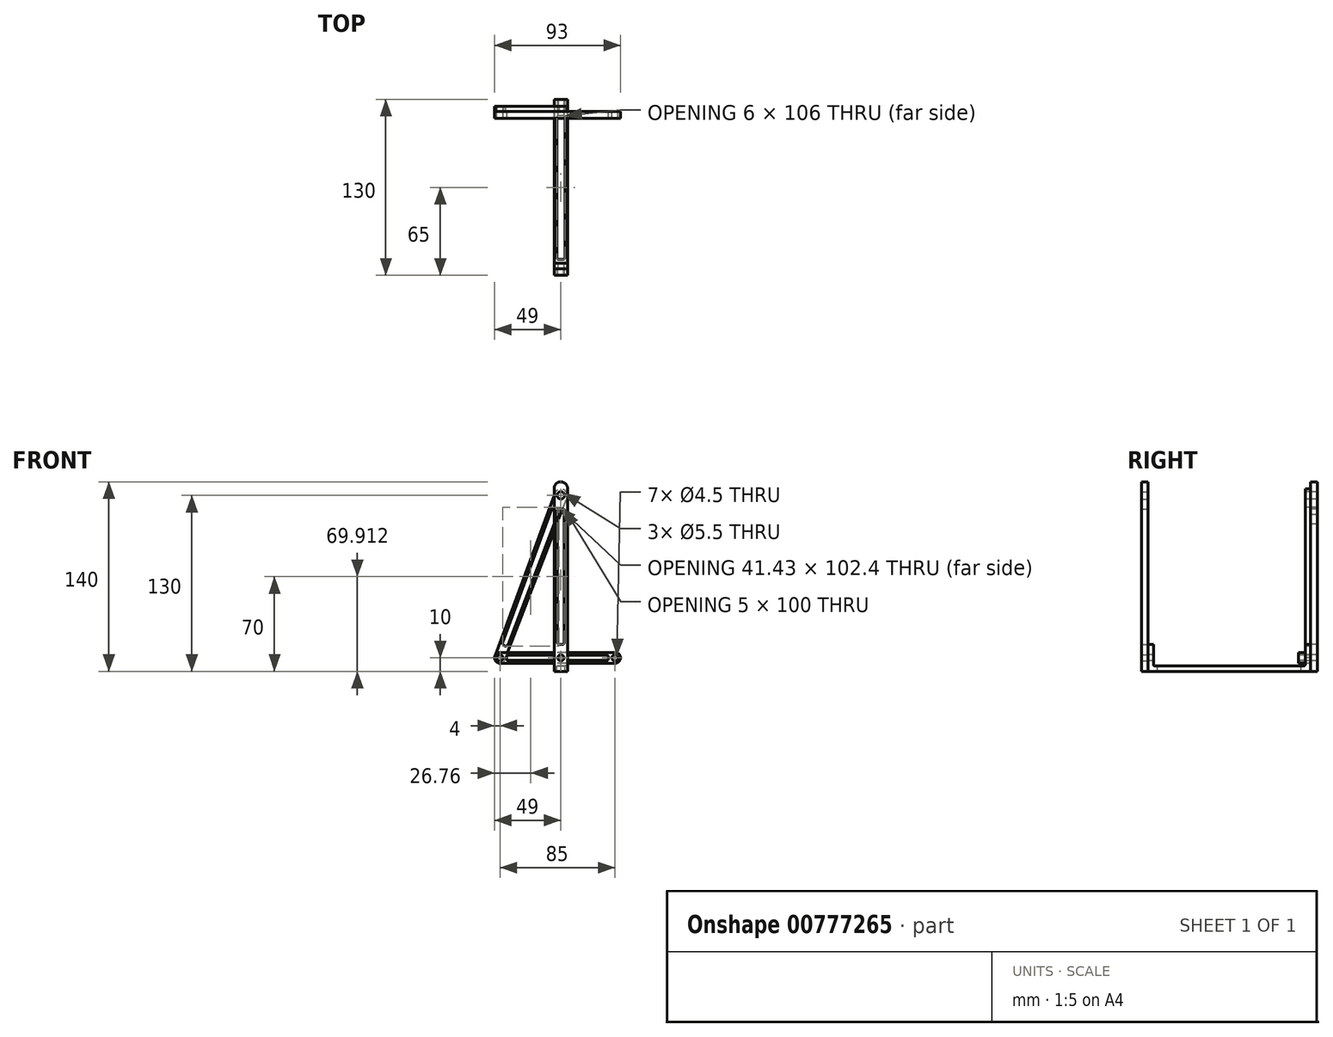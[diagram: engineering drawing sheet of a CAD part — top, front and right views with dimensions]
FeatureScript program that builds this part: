
annotation { "Feature Type Name" : "Feature", "Feature Type Description" : "" }
export const myFeature = defineFeature(function(context is Context, id is Id, definition is map)
    precondition{}
    {
        {
            var Q0;
            Q0=qCreatedBy(makeId("Front.planeOp"),FACE);
            var sketch = newSketch(context, id + "F0", { "sketchPlane" : qUnion([Q0])});
            skLineSegment(sketch, "E0", {"start": v(0, 0) * mm, "end": v(10, 0) * mm});
            skLineSegment(sketch, "E1", {"start": v(10, 0) * mm, "end": v(10, 135) * mm});
            skLineSegment(sketch, "E2", {"start": v(5, 140) * mm, "end": v(5, 140) * mm});
            skLineSegment(sketch, "E3", {"start": v(0, 135) * mm, "end": v(0, 0) * mm});
            skLineSegment(sketch, "E4", {"start": v(5, 140) * mm, "end": v(5, 130) * mm});
            skLineSegment(sketch, "E5", {"start": v(5, 130) * mm, "end": v(5, 10) * mm});
            skCircle(sketch, "E6", {"center": v(5, 130) * mm, "radius": 2.75 * mm});
            skCircle(sketch, "E7", {"center": v(5, 10) * mm, "radius": 2.25 * mm});
            skLineSegment(sketch, "E8", {"start": v(0, 70) * mm, "end": v(10, 70) * mm});
            skLineSegment(sketch, "E9.bottom", {"start": v(6.5, 20) * mm, "end": v(3.5, 20) * mm});
            skLineSegment(sketch, "E9.top", {"start": v(6.5, 120) * mm, "end": v(3.5, 120) * mm});
            skLineSegment(sketch, "E9.left", {"start": v(7.5, 21) * mm, "end": v(7.5, 119) * mm});
            skLineSegment(sketch, "E9.right", {"start": v(2.5, 21) * mm, "end": v(2.5, 119) * mm});
            skPoint(sketch, "E9.middle", {"position": v(5, 70) * mm});
            skPoint(sketch, "E10.visualSharp", {"position": v(0, 140) * mm});
            skArc(sketch, "E10.filletArc", {"start": v(5, 140) * mm, "mid": v(1.46, 138.54) * mm, "end": v(0, 135) * mm});
            skPoint(sketch, "E11.visualSharp", {"position": v(10, 140) * mm});
            skArc(sketch, "E11.filletArc", {"start": v(10, 135) * mm, "mid": v(8.54, 138.54) * mm, "end": v(5, 140) * mm});
            skPoint(sketch, "E12.visualSharp", {"position": v(2.5, 20) * mm});
            skArc(sketch, "E12.filletArc", {"start": v(2.5, 21) * mm, "mid": v(2.8, 20.3) * mm, "end": v(3.5, 20) * mm});
            skPoint(sketch, "E13.visualSharp", {"position": v(7.5, 20) * mm});
            skArc(sketch, "E13.filletArc", {"start": v(6.5, 20) * mm, "mid": v(7.2, 20.3) * mm, "end": v(7.5, 21) * mm});
            skPoint(sketch, "E14.visualSharp", {"position": v(2.5, 120) * mm});
            skArc(sketch, "E14.filletArc", {"start": v(3.5, 120) * mm, "mid": v(2.8, 119.7) * mm, "end": v(2.5, 119) * mm});
            skPoint(sketch, "E15.visualSharp", {"position": v(7.5, 120) * mm});
            skArc(sketch, "E15.filletArc", {"start": v(7.5, 119) * mm, "mid": v(7.2, 119.7) * mm, "end": v(6.5, 120) * mm});
            skSolve(sketch);
        }
        {
            var Q0;
            {var subQ5=sQuery(id+"F0.wireOp",EDGE,"E11.filletArc");Q0=makeQuery(id+"F0.imprint","IMPRINT",FACE,{"disambiguationData":[TD([[makeQuery(id+"F0.imprint","IMPRINT",EDGE,{"derivedFrom":subQ5}),1.0]])]});}
            var Q1;
            {var subQ5=sQuery(id+"F0.wireOp",EDGE,"E10.filletArc");Q1=makeQuery(id+"F0.imprint","IMPRINT",FACE,{"disambiguationData":[TD([[makeQuery(id+"F0.imprint","IMPRINT",EDGE,{"derivedFrom":subQ5}),1.0]])]});}
            var Q2;
            {var subQ13=sQuery(id+"F0.wireOp",EDGE,"E0");Q2=makeQuery(id+"F0.imprint","IMPRINT",FACE,{"disambiguationData":[TD([[makeQuery(id+"F0.imprint","IMPRINT",EDGE,{"derivedFrom":subQ13}),1.0]])]});}
            extrude(context, id + "F1", {"entities" : qUnion([Q0, Q1, Q2]), "depth" : 5 * mm, "offsetDistance" : 25 * mm});
        }
        {
            var Q0;
            Q0=qCreatedBy(makeId("Right.planeOp"),FACE);
            var sketch = newSketch(context, id + "F2", { "sketchPlane" : qUnion([Q0])});
            skLineSegment(sketch, "E16", {"start": v(0, 0) * mm, "end": v(60, 0) * mm});
            skLineSegment(sketch, "E17", {"start": v(60, 0) * mm, "end": v(60, 100) * mm});
            skSolve(sketch);
        }
        {
            var Q0;
            Q0=sQuery(id+"F2.wireOp",EDGE,"E17");
            cPlane(context, id + "F3", {"entities" : qUnion([Q0]), "cplaneType" : CPlaneType.LINE_ANGLE, "offset" : 25 * mm, "angle" : 90 * degree, "width" : 150 * mm, "height" : 150 * mm});
        }
        {
            var Q0;
            Q0=makeQuery(id+"F1.opExtrude","SWEPT_BODY",BODY,{"disambiguationData":[OSD([sQuery(id+"F0.wireOp",EDGE,"E0"),sQuery(id+"F0.wireOp",EDGE,"E1"),sQuery(id+"F0.wireOp",EDGE,"E3"),sQuery(id+"F0.wireOp",EDGE,"E6"),sQuery(id+"F0.wireOp",EDGE,"E7"),sQuery(id+"F0.wireOp",EDGE,"E9.bottom"),sQuery(id+"F0.wireOp",EDGE,"E9.top"),sQuery(id+"F0.wireOp",EDGE,"E9.left"),sQuery(id+"F0.wireOp",EDGE,"E9.right"),sQuery(id+"F0.wireOp",EDGE,"E10.filletArc"),sQuery(id+"F0.wireOp",EDGE,"E11.filletArc"),sQuery(id+"F0.wireOp",EDGE,"E12.filletArc"),sQuery(id+"F0.wireOp",EDGE,"E13.filletArc"),sQuery(id+"F0.wireOp",EDGE,"E14.filletArc"),sQuery(id+"F0.wireOp",EDGE,"E15.filletArc")])]});
            var Q1;
            Q1=qCreatedBy(id+"F3.planeOp",FACE);
            mirror(context, id + "F4", {"entities" : qUnion([Q0]), "mirrorPlane" : qUnion([Q1])});
        }
        {
            var Q0;
            Q0=qCreatedBy(makeId("Right.planeOp"),FACE);
            var sketch = newSketch(context, id + "F5", { "sketchPlane" : qUnion([Q0])});
            skLineSegment(sketch, "E18", {"start": v(0, 0) * mm, "end": v(120, 0) * mm});
            skLineSegment(sketch, "E19", {"start": v(120, 0) * mm, "end": v(120, 20) * mm});
            skLineSegment(sketch, "E20", {"start": v(120, 20) * mm, "end": v(0, 20) * mm});
            skLineSegment(sketch, "E21", {"start": v(0, 20) * mm, "end": v(0, 0) * mm});
            skLineSegment(sketch, "E22.0", {"start": v(116, 5) * mm, "end": v(116, 15) * mm});
            skLineSegment(sketch, "E22.1", {"start": v(5, 4) * mm, "end": v(115, 4) * mm});
            skLineSegment(sketch, "E22.2", {"start": v(4, 15) * mm, "end": v(4, 5) * mm});
            skPoint(sketch, "E23.visualSharp", {"position": v(116, 16) * mm});
            skPoint(sketch, "E24.visualSharp", {"position": v(4, 4) * mm});
            skArc(sketch, "E24.filletArc", {"start": v(4, 5) * mm, "mid": v(4.3, 4.3) * mm, "end": v(5, 4) * mm});
            skPoint(sketch, "E25.visualSharp", {"position": v(116, 4) * mm});
            skArc(sketch, "E25.filletArc", {"start": v(115, 4) * mm, "mid": v(115.7, 4.3) * mm, "end": v(116, 5) * mm});
            skLineSegment(sketch, "E26", {"start": v(116, 15) * mm, "end": v(116, 20) * mm});
            skLineSegment(sketch, "E27", {"start": v(4, 15) * mm, "end": v(4, 20) * mm});
            skSolve(sketch);
        }
        {
            var Q0;
            Q0=makeQuery(id+"F5.imprint","IMPRINT",FACE,{"disambiguationData":[TD([[makeQuery(id+"F5.imprint","IMPRINT",EDGE,{"derivedFrom":sQuery(id+"F5.wireOp",EDGE,"E18")}),1.0]])]});
            extrude(context, id + "F6", {"entities" : qUnion([Q0]), "depth" : 10 * mm, "offsetDistance" : 25 * mm});
        }
        {
            var Q0;
            Q0=makeQuery(id+"F6.opExtrude","SWEPT_FACE",FACE,{"disambiguationData":[OSD([sQuery(id+"F5.wireOp",EDGE,"E22.1")])]});
            var sketch = newSketch(context, id + "F7", { "sketchPlane" : qUnion([Q0])});
            skLineSegment(sketch, "E28.0", {"start": v(2, 112) * mm, "end": v(2, 8) * mm});
            skLineSegment(sketch, "E28.1", {"start": v(7, 113) * mm, "end": v(3, 113) * mm});
            skLineSegment(sketch, "E28.2", {"start": v(8, 8) * mm, "end": v(8, 112) * mm});
            skLineSegment(sketch, "E28.3", {"start": v(3, 7) * mm, "end": v(7, 7) * mm});
            skPoint(sketch, "E29.visualSharp", {"position": v(2, 7) * mm});
            skArc(sketch, "E29.filletArc", {"start": v(2, 8) * mm, "mid": v(2.3, 7.3) * mm, "end": v(3, 7) * mm});
            skPoint(sketch, "E30.visualSharp", {"position": v(8, 7) * mm});
            skArc(sketch, "E30.filletArc", {"start": v(7, 7) * mm, "mid": v(7.7, 7.3) * mm, "end": v(8, 8) * mm});
            skPoint(sketch, "E31.visualSharp", {"position": v(8, 113) * mm});
            skArc(sketch, "E31.filletArc", {"start": v(8, 112) * mm, "mid": v(7.7, 112.7) * mm, "end": v(7, 113) * mm});
            skPoint(sketch, "E32.visualSharp", {"position": v(2, 113) * mm});
            skArc(sketch, "E32.filletArc", {"start": v(3, 113) * mm, "mid": v(2.3, 112.7) * mm, "end": v(2, 112) * mm});
            skSolve(sketch);
        }
        {
            var Q0;
            Q0=makeQuery(id+"F7.imprint","IMPRINT",FACE,{"disambiguationData":[TD([[makeQuery(id+"F7.imprint","IMPRINT",EDGE,{"derivedFrom":sQuery(id+"F7.wireOp",EDGE,"E28.0")}),1.0]])]});
            extrude(context, id + "F8", {"entities" : qUnion([Q0]), "operationType" : NewBodyOperationType.REMOVE, "oppositeDirection" : true, "depth" : 25 * mm, "offsetDistance" : 25 * mm});
        }
        {
            var Q0;
            Q0=makeQuery(id+"F1.opExtrude","CAP_FACE",FACE,{"disambiguationData":[OSD([sQuery(id+"F0.wireOp",EDGE,"E0"),sQuery(id+"F0.wireOp",EDGE,"E1"),sQuery(id+"F0.wireOp",EDGE,"E3"),sQuery(id+"F0.wireOp",EDGE,"E6"),sQuery(id+"F0.wireOp",EDGE,"E7"),sQuery(id+"F0.wireOp",EDGE,"E9.bottom"),sQuery(id+"F0.wireOp",EDGE,"E9.top"),sQuery(id+"F0.wireOp",EDGE,"E9.left"),sQuery(id+"F0.wireOp",EDGE,"E9.right"),sQuery(id+"F0.wireOp",EDGE,"E10.filletArc"),sQuery(id+"F0.wireOp",EDGE,"E11.filletArc"),sQuery(id+"F0.wireOp",EDGE,"E12.filletArc"),sQuery(id+"F0.wireOp",EDGE,"E13.filletArc"),sQuery(id+"F0.wireOp",EDGE,"E14.filletArc"),sQuery(id+"F0.wireOp",EDGE,"E15.filletArc")])],"isStart":false});
            var sketch = newSketch(context, id + "F9", { "sketchPlane" : qUnion([Q0])});
            skCircle(sketch, "E33.0", {"center": v(5, 10) * mm, "radius": 2.25 * mm});
            skSolve(sketch);
        }
        {
            var Q0;
            Q0=makeQuery(id+"F9.imprint","IMPRINT",FACE,{"disambiguationData":[TD([[makeQuery(id+"F9.imprint","IMPRINT",EDGE,{"derivedFrom":sQuery(id+"F9.wireOp",EDGE,"E33.0")}),1.0]])]});
            extrude(context, id + "F10", {"entities" : qUnion([Q0]), "operationType" : NewBodyOperationType.REMOVE, "endBound" : BoundingType.THROUGH_ALL, "oppositeDirection" : true, "depth" : 25 * mm, "offsetDistance" : 25 * mm});
        }
        {
            var Q0;
            Q0=makeQuery(id+"F6.opExtrude","SWEPT_FACE",FACE,{"disambiguationData":[OSD([sQuery(id+"F5.wireOp",EDGE,"E22.0"),sQuery(id+"F5.wireOp",EDGE,"E26")])]});
            var sketch = newSketch(context, id + "F11", { "sketchPlane" : qUnion([Q0])});
            skCircle(sketch, "E34", {"center": v(5, 10) * mm, "radius": 4 * mm});
            skLineSegment(sketch, "E35", {"start": v(5, 10) * mm, "end": v(5, 14) * mm});
            skLineSegment(sketch, "E36", {"start": v(5, 14) * mm, "end": v(0, 14) * mm});
            skLineSegment(sketch, "E37", {"start": v(5, 10) * mm, "end": v(5, 6) * mm});
            skLineSegment(sketch, "E38", {"start": v(5, 6) * mm, "end": v(0, 6) * mm});
            skLineSegment(sketch, "E39", {"start": v(0, 6) * mm, "end": v(-40, 6) * mm});
            skLineSegment(sketch, "E40", {"start": v(-40, 6) * mm, "end": v(-40, 10) * mm});
            skCircle(sketch, "E41", {"center": v(-40, 10) * mm, "radius": 4 * mm});
            skCircle(sketch, "E42", {"center": v(-40, 10) * mm, "radius": 2.25 * mm});
            skLineSegment(sketch, "E43", {"start": v(0, 14) * mm, "end": v(-40, 14) * mm});
            skLineSegment(sketch, "E44", {"start": v(-40, 10) * mm, "end": v(-35, 10) * mm});
            skLineSegment(sketch, "E45", {"start": v(-35, 10) * mm, "end": v(-45, 10) * mm});
            skLineSegment(sketch, "E46", {"start": v(5, 14) * mm, "end": v(45, 14) * mm});
            skLineSegment(sketch, "E47", {"start": v(45, 14) * mm, "end": v(45, 9) * mm});
            skLineSegment(sketch, "E48", {"start": v(45, 9) * mm, "end": v(45, 6) * mm});
            skLineSegment(sketch, "E49", {"start": v(45, 6) * mm, "end": v(5, 6) * mm});
            skCircle(sketch, "E50", {"center": v(45, 10) * mm, "radius": 4 * mm});
            skCircle(sketch, "E51", {"center": v(45, 10) * mm, "radius": 2.25 * mm});
            skLineSegment(sketch, "E52.bottom", {"start": v(39, 8) * mm, "end": v(11, 8) * mm});
            skLineSegment(sketch, "E52.top", {"start": v(39, 12) * mm, "end": v(11, 12) * mm});
            skLineSegment(sketch, "E52.left", {"start": v(40, 9) * mm, "end": v(40, 11) * mm});
            skLineSegment(sketch, "E52.right", {"start": v(10, 9) * mm, "end": v(10, 11) * mm});
            skPoint(sketch, "E52.middle", {"position": v(25, 10) * mm});
            skPoint(sketch, "E52.middle.positionSnap0", {"position": v(25, 14) * mm});
            skPoint(sketch, "E52.centerSnap0", {"position": v(25, 14) * mm});
            skPoint(sketch, "E53.visualSharp", {"position": v(10, 12) * mm});
            skArc(sketch, "E53.filletArc", {"start": v(11, 12) * mm, "mid": v(10.3, 11.7) * mm, "end": v(10, 11) * mm});
            skPoint(sketch, "E54.visualSharp", {"position": v(10, 8) * mm});
            skArc(sketch, "E54.filletArc", {"start": v(10, 9) * mm, "mid": v(10.3, 8.3) * mm, "end": v(11, 8) * mm});
            skPoint(sketch, "E55.visualSharp", {"position": v(40, 8) * mm});
            skArc(sketch, "E55.filletArc", {"start": v(39, 8) * mm, "mid": v(39.7, 8.3) * mm, "end": v(40, 9) * mm});
            skPoint(sketch, "E56.visualSharp", {"position": v(40, 12) * mm});
            skArc(sketch, "E56.filletArc", {"start": v(40, 11) * mm, "mid": v(39.7, 11.7) * mm, "end": v(39, 12) * mm});
            skSolve(sketch);
        }
        {
            var Q0;
            {var subQ0=sQuery(id+"F11.wireOp",EDGE,"E35");var subQ1=sQuery(id+"F11.wireOp",EDGE,"E34");var subQ2=makeQuery(id+"F11.imprint","INTERSECT",VERTEX,{"derivedFrom":[subQ1,subQ0,sQuery(id+"F11.wireOp",EDGE,"E36")]});Q0=makeQuery(id+"F11.imprint","IMPRINT",FACE,{"disambiguationData":[TD([[makeQuery(id+"F11.imprint","IMPRINT",EDGE,{"disambiguationData":[TD([[subQ2,-1.0]])],"derivedFrom":subQ1}),1.0]])]});}
            var Q1;
            {var subQ0=sQuery(id+"F11.wireOp",EDGE,"E35");var subQ1=sQuery(id+"F11.wireOp",EDGE,"E34");var subQ2=makeQuery(id+"F11.imprint","INTERSECT",VERTEX,{"derivedFrom":[subQ1,subQ0,sQuery(id+"F11.wireOp",EDGE,"E36")]});Q1=makeQuery(id+"F11.imprint","IMPRINT",FACE,{"disambiguationData":[TD([[makeQuery(id+"F11.imprint","IMPRINT",EDGE,{"disambiguationData":[TD([[subQ2,1.0]])],"derivedFrom":subQ1}),1.0]])]});}
            var Q2;
            {var subQ0=sQuery(id+"F11.wireOp",EDGE,"E36");Q2=makeQuery(id+"F11.imprint","IMPRINT",FACE,{"disambiguationData":[TD([[makeQuery(id+"F11.imprint","IMPRINT",EDGE,{"derivedFrom":subQ0}),1.0]])]});}
            var Q3;
            {var subQ1=sQuery(id+"F11.wireOp",EDGE,"E39");Q3=makeQuery(id+"F11.imprint","IMPRINT",FACE,{"disambiguationData":[TD([[makeQuery(id+"F11.imprint","IMPRINT",EDGE,{"derivedFrom":subQ1}),-1.0]])]});}
            var Q4;
            {var subQ1=sQuery(id+"F11.wireOp",EDGE,"E40");var subQ3=sQuery(id+"F11.wireOp",EDGE,"E42");var subQ4=makeQuery(id+"F11.imprint","INTERSECT",VERTEX,{"derivedFrom":[subQ1,subQ3]});Q4=makeQuery(id+"F11.imprint","IMPRINT",FACE,{"disambiguationData":[TD([[makeQuery(id+"F11.imprint","IMPRINT",EDGE,{"disambiguationData":[TD([[subQ4,-1.0]])],"derivedFrom":subQ3}),-1.0]])]});}
            var Q5;
            {var subQ1=sQuery(id+"F11.wireOp",EDGE,"E40");var subQ3=sQuery(id+"F11.wireOp",EDGE,"E42");var subQ4=makeQuery(id+"F11.imprint","INTERSECT",VERTEX,{"derivedFrom":[subQ1,subQ3]});Q5=makeQuery(id+"F11.imprint","IMPRINT",FACE,{"disambiguationData":[TD([[makeQuery(id+"F11.imprint","IMPRINT",EDGE,{"disambiguationData":[TD([[subQ4,1.0]])],"derivedFrom":subQ3}),-1.0]])]});}
            var Q6;
            {var subQ1=sQuery(id+"F11.wireOp",EDGE,"E41");var subQ6=makeQuery(id+"F11.imprint","INTERSECT",VERTEX,{"derivedFrom":[subQ1,sQuery(id+"F11.wireOp",EDGE,"E43")]});Q6=makeQuery(id+"F11.imprint","IMPRINT",FACE,{"disambiguationData":[TD([[makeQuery(id+"F11.imprint","IMPRINT",EDGE,{"disambiguationData":[TD([[subQ6,1.0]])],"derivedFrom":subQ1}),1.0]])]});}
            extrude(context, id + "F12", {"entities" : qUnion([Q0, Q1, Q2, Q3, Q4, Q5, Q6]), "depth" : 5 * mm, "offsetDistance" : 25 * mm});
        }
        {
            var Q0;
            Q0=makeQuery(id+"F12.opExtrude","CAP_FACE",FACE,{"disambiguationData":[OSD([sQuery(id+"F5.wireOp",EDGE,"E22.0"),sQuery(id+"F5.wireOp",EDGE,"E26"),sQuery(id+"F9.wireOp",EDGE,"E33.0"),sQuery(id+"F11.wireOp",EDGE,"E34"),sQuery(id+"F11.wireOp",EDGE,"E36"),sQuery(id+"F11.wireOp",EDGE,"E38"),sQuery(id+"F11.wireOp",EDGE,"E39"),sQuery(id+"F11.wireOp",EDGE,"E41"),sQuery(id+"F11.wireOp",EDGE,"E42"),sQuery(id+"F11.wireOp",EDGE,"E43")])],"isStart":false});
            var sketch = newSketch(context, id + "F13", { "sketchPlane" : qUnion([Q0])});
            skCircle(sketch, "E57", {"center": v(5, 10) * mm, "radius": 2 * mm});
            skLineSegment(sketch, "E58", {"start": v(-40, 10) * mm, "end": v(5, 10) * mm});
            skLineSegment(sketch, "E59.bottom", {"start": v(-1, 8) * mm, "end": v(-34, 8) * mm});
            skLineSegment(sketch, "E59.top", {"start": v(-1, 12) * mm, "end": v(-34, 12) * mm});
            skLineSegment(sketch, "E59.left", {"start": v(0, 9) * mm, "end": v(0, 11) * mm});
            skLineSegment(sketch, "E59.right", {"start": v(-35, 9) * mm, "end": v(-35, 11) * mm});
            skPoint(sketch, "E59.middle", {"position": v(-17.5, 10) * mm});
            skPoint(sketch, "E60.visualSharp", {"position": v(-35, 12) * mm});
            skArc(sketch, "E60.filletArc", {"start": v(-34, 12) * mm, "mid": v(-34.7, 11.7) * mm, "end": v(-35, 11) * mm});
            skPoint(sketch, "E61.visualSharp", {"position": v(-35, 8) * mm});
            skArc(sketch, "E61.filletArc", {"start": v(-35, 9) * mm, "mid": v(-34.7, 8.3) * mm, "end": v(-34, 8) * mm});
            skPoint(sketch, "E62.visualSharp", {"position": v(0, 8) * mm});
            skArc(sketch, "E62.filletArc", {"start": v(-1, 8) * mm, "mid": v(-0.3, 8.3) * mm, "end": v(0, 9) * mm});
            skPoint(sketch, "E63.visualSharp", {"position": v(0, 12) * mm});
            skArc(sketch, "E63.filletArc", {"start": v(0, 11) * mm, "mid": v(-0.3, 11.7) * mm, "end": v(-1, 12) * mm});
            skSolve(sketch);
        }
        {
            var Q0;
            Q0=makeQuery(id+"F13.imprint","IMPRINT",FACE,{"disambiguationData":[TD([[makeQuery(id+"F13.imprint","IMPRINT",EDGE,{"derivedFrom":sQuery(id+"F13.wireOp",EDGE,"E59.top")}),1.0]])]});
            var Q1;
            Q1=makeQuery(id+"F13.imprint","IMPRINT",FACE,{"disambiguationData":[TD([[makeQuery(id+"F13.imprint","IMPRINT",EDGE,{"derivedFrom":sQuery(id+"F13.wireOp",EDGE,"E59.bottom")}),-1.0]])]});
            extrude(context, id + "F14", {"entities" : qUnion([Q0, Q1]), "operationType" : NewBodyOperationType.REMOVE, "oppositeDirection" : true, "depth" : 25 * mm, "offsetDistance" : 25 * mm});
        }
        {
            var Q0;
            Q0=makeQuery(id+"F12.opExtrude","SWEPT_BODY",BODY,{"disambiguationData":[OSD([sQuery(id+"F5.wireOp",EDGE,"E22.0"),sQuery(id+"F5.wireOp",EDGE,"E26"),sQuery(id+"F9.wireOp",EDGE,"E33.0"),sQuery(id+"F11.wireOp",EDGE,"E34"),sQuery(id+"F11.wireOp",EDGE,"E36"),sQuery(id+"F11.wireOp",EDGE,"E38"),sQuery(id+"F11.wireOp",EDGE,"E39"),sQuery(id+"F11.wireOp",EDGE,"E41"),sQuery(id+"F11.wireOp",EDGE,"E42"),sQuery(id+"F11.wireOp",EDGE,"E43")])]});
            transform(context, id + "F15", {"entities" : qUnion([Q0]), "transformType" : TransformType.TRANSLATION_3D, "dx" : 0 * mm, "dy" : 0 * mm, "dz" : 0 * mm, "makeCopy" : true});
        }
        {
            var Q0;
            {var subQ0=sQuery(id+"F11.wireOp",EDGE,"E50");var subQ1=sQuery(id+"F11.wireOp",EDGE,"E46");var subQ2=makeQuery(id+"F11.imprint","INTERSECT",VERTEX,{"derivedFrom":[subQ1,sQuery(id+"F11.wireOp",EDGE,"E47"),subQ0]});Q0=makeQuery(id+"F11.imprint","IMPRINT",FACE,{"disambiguationData":[TD([[makeQuery(id+"F11.imprint","IMPRINT",EDGE,{"disambiguationData":[TD([[subQ2,1.0]])],"derivedFrom":subQ1}),-1.0]])]});}
            var Q1;
            {var subQ0=sQuery(id+"F11.wireOp",EDGE,"E46");var subQ5=makeQuery(id+"F6.opExtrude","CAP_EDGE",EDGE,{"disambiguationData":[OSD([sQuery(id+"F5.wireOp",EDGE,"E22.0"),sQuery(id+"F5.wireOp",EDGE,"E26")])],"isStart":false});var subQ6=makeQuery(id+"F11.imprint","INTERSECT",VERTEX,{"derivedFrom":[subQ5,subQ0]});Q1=makeQuery(id+"F11.imprint","IMPRINT",FACE,{"disambiguationData":[TD([[makeQuery(id+"F11.imprint","IMPRINT",EDGE,{"disambiguationData":[TD([[subQ6,1.0]])],"derivedFrom":subQ0}),-1.0]])]});}
            var Q2;
            {var subQ1=sQuery(id+"F11.wireOp",EDGE,"E47");var subQ3=sQuery(id+"F11.wireOp",EDGE,"E51");var subQ4=makeQuery(id+"F11.imprint","INTERSECT",VERTEX,{"derivedFrom":[subQ1,subQ3]});Q2=makeQuery(id+"F11.imprint","IMPRINT",FACE,{"disambiguationData":[TD([[makeQuery(id+"F11.imprint","IMPRINT",EDGE,{"disambiguationData":[TD([[subQ4,-1.0]])],"derivedFrom":subQ3}),-1.0]])]});}
            var Q3;
            {var subQ1=sQuery(id+"F11.wireOp",EDGE,"E47");var subQ3=sQuery(id+"F11.wireOp",EDGE,"E51");var subQ4=makeQuery(id+"F11.imprint","INTERSECT",VERTEX,{"derivedFrom":[subQ1,subQ3]});Q3=makeQuery(id+"F11.imprint","IMPRINT",FACE,{"disambiguationData":[TD([[makeQuery(id+"F11.imprint","IMPRINT",EDGE,{"disambiguationData":[TD([[subQ4,1.0]])],"derivedFrom":subQ3}),-1.0]])]});}
            extrude(context, id + "F16", {"entities" : qUnion([Q0, Q1, Q2, Q3]), "operationType" : NewBodyOperationType.ADD, "depth" : 5 * mm, "offsetDistance" : 25 * mm});
        }
        {
            var Q0;
            {var subQ1=sQuery(id+"F11.wireOp",EDGE,"E39");Q0=makeQuery(id+"F11.imprint","IMPRINT",FACE,{"disambiguationData":[TD([[makeQuery(id+"F11.imprint","IMPRINT",EDGE,{"derivedFrom":subQ1}),-1.0]])]});}
            var sketch = newSketch(context, id + "F17", { "sketchPlane" : qUnion([Q0])});
            skCircle(sketch, "E64.0", {"center": v(-40, 10) * mm, "radius": 2.25 * mm});
            skCircle(sketch, "E65.0", {"center": v(-40, 10) * mm, "radius": 4 * mm});
            skCircle(sketch, "E66.0", {"center": v(5, 130) * mm, "radius": 2.75 * mm});
            skCircle(sketch, "E67.0", {"center": v(5, 130) * mm, "radius": 4.75 * mm});
            skLineSegment(sketch, "E68", {"start": v(-43.48, 11.98) * mm, "end": v(0.54, 131.64) * mm});
            skLineSegment(sketch, "E69", {"start": v(-36, 10) * mm, "end": v(9.43, 128.3) * mm});
            skSolve(sketch);
        }
        {
            var Q0;
            {var subQ5=sQuery(id+"F17.wireOp",EDGE,"E68");Q0=makeQuery(id+"F17.imprint","IMPRINT",FACE,{"disambiguationData":[TD([[makeQuery(id+"F17.imprint","IMPRINT",EDGE,{"derivedFrom":subQ5}),-1.0]])]});}
            var Q1;
            Q1=makeQuery(id+"F17.imprint","IMPRINT",FACE,{"disambiguationData":[TD([[makeQuery(id+"F17.imprint","IMPRINT",EDGE,{"derivedFrom":sQuery(id+"F17.wireOp",EDGE,"E64.0")}),-1.0]])]});
            var Q2;
            {var subQ0=sQuery(id+"F17.wireOp",EDGE,"E65.0");var subQ1=makeQuery(id+"F11.imprint","IMPRINT",EDGE,{"derivedFrom":sQuery(id+"F11.wireOp",EDGE,"E43")});var subQ2=makeQuery(id+"F17.imprint","INTERSECT",VERTEX,{"derivedFrom":[subQ1,subQ0]});Q2=makeQuery(id+"F17.imprint","IMPRINT",FACE,{"disambiguationData":[TD([[makeQuery(id+"F17.imprint","IMPRINT",EDGE,{"disambiguationData":[TD([[subQ2,1.0]])],"derivedFrom":subQ0}),-1.0]])]});}
            var Q3;
            Q3=makeQuery(id+"F17.imprint","IMPRINT",FACE,{"disambiguationData":[TD([[makeQuery(id+"F17.imprint","IMPRINT",EDGE,{"derivedFrom":sQuery(id+"F17.wireOp",EDGE,"E66.0")}),-1.0]])]});
            extrude(context, id + "F18", {"entities" : qUnion([Q0, Q1, Q2, Q3]), "oppositeDirection" : true, "depth" : 4 * mm, "offsetDistance" : 25 * mm});
        }
        {
            var Q0;
            Q0=makeQuery(id+"F18.opExtrude","CAP_FACE",FACE,{"disambiguationData":[OSD([sQuery(id+"F17.wireOp",EDGE,"E64.0"),sQuery(id+"F17.wireOp",EDGE,"E65.0"),sQuery(id+"F17.wireOp",EDGE,"E66.0"),sQuery(id+"F17.wireOp",EDGE,"E67.0"),sQuery(id+"F17.wireOp",EDGE,"E68"),sQuery(id+"F17.wireOp",EDGE,"E69")])],"isStart":true});
            var sketch = newSketch(context, id + "F19", { "sketchPlane" : qUnion([Q0])});
            skLineSegment(sketch, "E70", {"start": v(-1.65, 119.8) * mm, "end": v(-37.83, 21.45) * mm});
            skLineSegment(sketch, "E71", {"start": v(-41.4, 11.76) * mm, "end": v(-37.75, 10) * mm});
            skLineSegment(sketch, "E72", {"start": v(-33.94, 20) * mm, "end": v(3.34, 117.92) * mm});
            skLineSegment(sketch, "E73", {"start": v(0.93, 120.98) * mm, "end": v(2.19, 120.5) * mm});
            skLineSegment(sketch, "E74", {"start": v(-36.65, 18.89) * mm, "end": v(-36.5, 18.83) * mm});
            skPoint(sketch, "E75.visualSharp", {"position": v(-0.96, 121.7) * mm});
            skArc(sketch, "E75.filletArc", {"start": v(0.93, 120.98) * mm, "mid": v(-0.6, 120.93) * mm, "end": v(-1.65, 119.8) * mm});
            skPoint(sketch, "E76.visualSharp", {"position": v(4.06, 119.8) * mm});
            skArc(sketch, "E76.filletArc", {"start": v(3.34, 117.92) * mm, "mid": v(3.3, 119.45) * mm, "end": v(2.19, 120.5) * mm});
            skPoint(sketch, "E77.visualSharp", {"position": v(-38.52, 19.58) * mm});
            skArc(sketch, "E77.filletArc", {"start": v(-37.83, 21.45) * mm, "mid": v(-37.77, 19.92) * mm, "end": v(-36.65, 18.89) * mm});
            skPoint(sketch, "E78.visualSharp", {"position": v(-34.65, 18.15) * mm});
            skArc(sketch, "E78.filletArc", {"start": v(-36.5, 18.83) * mm, "mid": v(-34.98, 18.89) * mm, "end": v(-33.94, 20) * mm});
            skSolve(sketch);
        }
        {
            var Q0;
            Q0=makeQuery(id+"F19.imprint","IMPRINT",FACE,{"disambiguationData":[TD([[makeQuery(id+"F19.imprint","IMPRINT",EDGE,{"derivedFrom":sQuery(id+"F19.wireOp",EDGE,"E70")}),1.0]])]});
            extrude(context, id + "F20", {"entities" : qUnion([Q0]), "operationType" : NewBodyOperationType.REMOVE, "oppositeDirection" : true, "depth" : 25 * mm, "offsetDistance" : 25 * mm});
        }
    });
